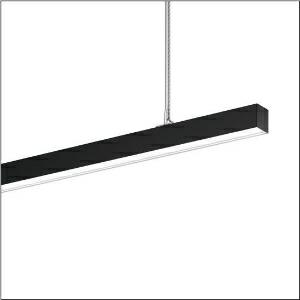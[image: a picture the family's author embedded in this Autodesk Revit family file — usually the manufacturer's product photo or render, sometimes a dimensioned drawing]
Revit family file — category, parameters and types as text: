
# Revit family: silica_r__21_51mx33da47bb_630a
name_source: partatom
category: Lighting Fixtures
units: mm (PartAtom-declared; Revit-internal decimal feet)

## family parameters
Cut with Voids When Loaded = No
Host = Face
Light Source = No
Part Type = Normal
Room Calculation Point = No
Round Connector Dimension = Use Diameter
Shared = No

## types (1)
- --- (1 x LED, 5910 lm, 38.4 W, 4000K)
    Apparent Load = 38 VA
    CIE Flux Codes = 78 96 99 55 100
    Color Rendering = 80
    Color Temperature = 4000K
    Default Elevation = 1800 mm
    Description = Silica® 21, office luminaire, primary optical cover: prismatic diffuser, of PMMA, CAT 2 (L<= 3000cd/m²), light emission: direct/indirect distribution, primary light characteristic: symmetric, installation type: suspended mounting, LED, rated luminous flux: 5.910lm, luminous efficacy: 154lm/W, light colour: 840, colour temperature: 4000K, control gear: DALI 2, with terminal, 3+2-pole, max. 2.5mm², mains connection: 220..240V, AC, 50/60Hz, rated input power: 38.4W, luminaire housing, of aluminium, matt jet black (RAL 9005), length: 1.204mm, width: 53mm, height: 53mm, protection rating (complete): IP20, insulation class (complete): insulation class I (protective earthing), certification: CE, permissible operating ambient temperature: 0..+35°C, standard: EN 50419, packaging unit: 1 piece
    Height = 53 mm
    Lamp = 1 x LED
    Lamp Light Flux = 5910 lm
    Lamp Power = 38.4 W
    Lamp count = 1
    Length = 1204 mm
    Luminous efficacy = 154 lm/W
    Manufacturer = Siteco
    ModVariant = No
    Model = 51MX33DA47BB
    Mounting Place = Ceiling
    Mounting Type = Pendant
    Number of Poles = 1
    OnlyDefault = Yes
    Power Factor = 1
    Product Name = Silica® 21
    Product group = office luminaire | ceiling pendant
    ProductGroupID = 903
    Protection Class = Protection class I
    Protection Degree = IP 20
    RLX_Detail_Level = 1
    RLX_Emergency_Light_Flux = 0 lm
    RLX_Emergency_Type = 0
    RLX_Emergency_Type_DB = No
    RlxData = <blob elided: 25837 chars, md5=ec559d61>
    Socket = socket
    Standby Power = 0 W
    System Light Flux = 5910 lm
    System Power = 38 W
    Type Comments = factory setting: luminous flux: 100 % | dim-lin: 254 | 322 mA
    Type Image = l_1335856.jpg
    URL = http://relux.com
    VarID = @adj_140275
    Voltage = 0 V
    Weight = 0.00 kg
    Width = 53 mm

## geometry (parser evidence)
native form markers: Blend x4, Sweep x14
no freeform markers — native parametric forms only
